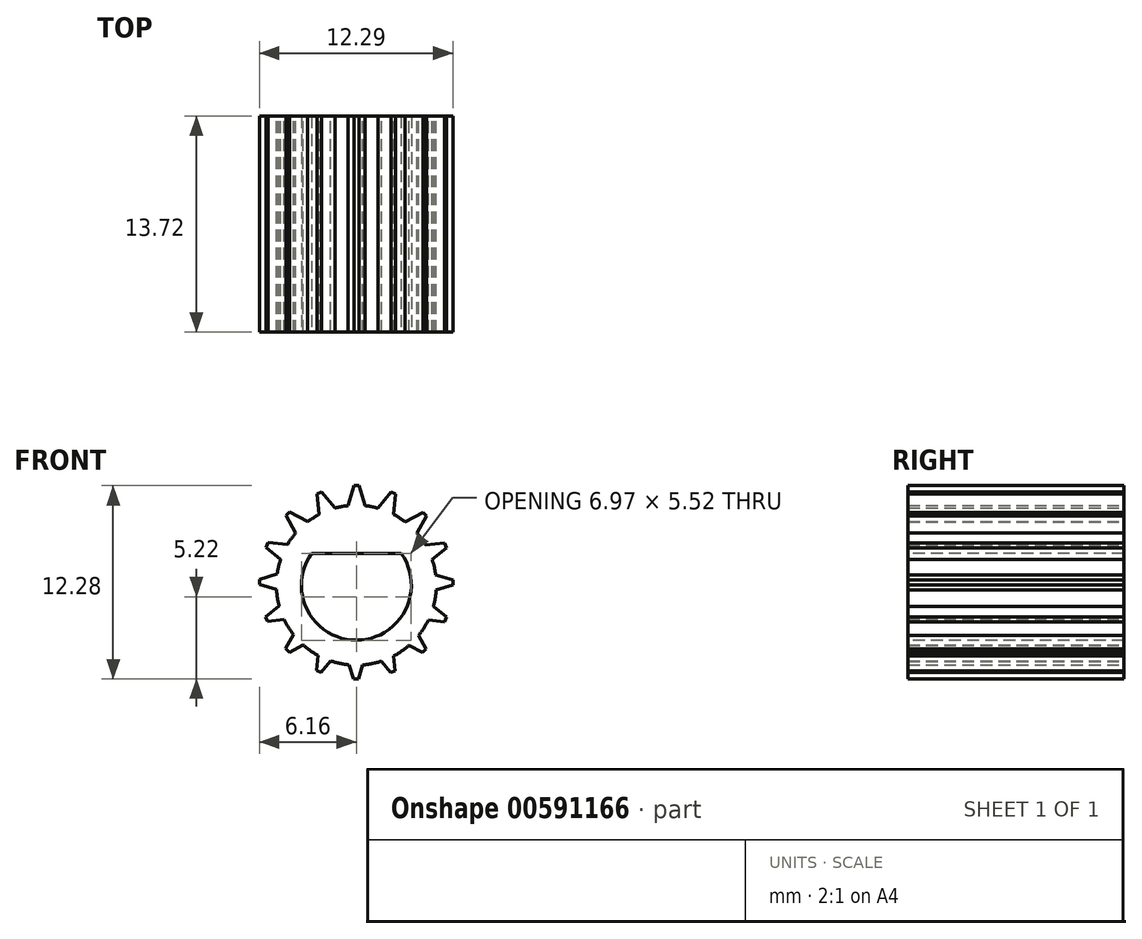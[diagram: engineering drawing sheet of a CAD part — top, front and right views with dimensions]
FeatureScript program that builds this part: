
annotation { "Feature Type Name" : "Feature", "Feature Type Description" : "" }
export const myFeature = defineFeature(function(context is Context, id is Id, definition is map)
    precondition{}
    {
        {
            var Q0;
            Q0=qCreatedBy(makeId("Front.planeOp"),FACE);
            var sketch = newSketch(context, id + "F0", { "sketchPlane" : qUnion([Q0])});
            skCircle(sketch, "E0", {"center": v(0, 0) * mm, "radius": 6.25 * mm});
            skLineSegment(sketch, "E1", {"start": v(0, 0) * mm, "end": v(0, 6.25) * mm, "construction": true});
            skLineSegment(sketch, "E2", {"start": v(0, 6.25) * mm, "end": v(0, 9.25) * mm});
            skLineSegment(sketch, "E3", {"start": v(0, 9.25) * mm, "end": v(-0.96, 9.25) * mm});
            skLineSegment(sketch, "E4", {"start": v(-0.96, 9.25) * mm, "end": v(-2.3, 5.81) * mm});
            skLineSegment(sketch, "E5.MirrorCS", {"start": v(0, 9.25) * mm, "end": v(0.96, 9.25) * mm});
            skLineSegment(sketch, "E6.MirrorCS", {"start": v(0.96, 9.25) * mm, "end": v(2.3, 5.81) * mm});
            skPoint(sketch, "E7.center", {"position": v(0, 1.25) * mm});
            skPoint(sketch, "E8.center", {"position": v(0, -1) * mm});
            skLineSegment(sketch, "E9.1.0", {"start": v(-8.5, 3.8) * mm, "end": v(-6.18, 0.91) * mm});
            skLineSegment(sketch, "E9.1.1", {"start": v(-8.01, 4.62) * mm, "end": v(-8.5, 3.8) * mm});
            skLineSegment(sketch, "E9.1.2", {"start": v(-7.53, 5.46) * mm, "end": v(-3.88, 4.9) * mm});
            skLineSegment(sketch, "E9.1.3", {"start": v(-8.01, 4.62) * mm, "end": v(-7.53, 5.46) * mm});
            skLineSegment(sketch, "E9.2.0", {"start": v(-7.53, -5.46) * mm, "end": v(-3.88, -4.9) * mm});
            skLineSegment(sketch, "E9.2.1", {"start": v(-8.01, -4.63) * mm, "end": v(-7.53, -5.46) * mm});
            skLineSegment(sketch, "E9.2.2", {"start": v(-8.5, -3.8) * mm, "end": v(-6.18, -0.91) * mm});
            skLineSegment(sketch, "E9.2.3", {"start": v(-8.01, -4.63) * mm, "end": v(-8.5, -3.8) * mm});
            skLineSegment(sketch, "E9.3.0", {"start": v(0.96, -9.25) * mm, "end": v(2.3, -5.81) * mm});
            skLineSegment(sketch, "E9.3.1", {"start": v(0, -9.25) * mm, "end": v(0.96, -9.25) * mm});
            skLineSegment(sketch, "E9.3.2", {"start": v(-0.96, -9.25) * mm, "end": v(-2.3, -5.81) * mm});
            skLineSegment(sketch, "E9.3.3", {"start": v(0, -9.25) * mm, "end": v(-0.96, -9.25) * mm});
            skLineSegment(sketch, "E9.4.0", {"start": v(8.5, -3.8) * mm, "end": v(6.18, -0.91) * mm});
            skLineSegment(sketch, "E9.4.1", {"start": v(8.01, -4.63) * mm, "end": v(8.5, -3.8) * mm});
            skLineSegment(sketch, "E9.4.2", {"start": v(7.53, -5.46) * mm, "end": v(3.88, -4.9) * mm});
            skLineSegment(sketch, "E9.4.3", {"start": v(8.01, -4.63) * mm, "end": v(7.53, -5.46) * mm});
            skLineSegment(sketch, "E9.5.0", {"start": v(7.53, 5.46) * mm, "end": v(3.88, 4.9) * mm});
            skLineSegment(sketch, "E9.5.1", {"start": v(8.01, 4.63) * mm, "end": v(7.53, 5.46) * mm});
            skLineSegment(sketch, "E9.5.2", {"start": v(8.5, 3.8) * mm, "end": v(6.18, 0.91) * mm});
            skLineSegment(sketch, "E9.5.3", {"start": v(8.01, 4.63) * mm, "end": v(8.5, 3.8) * mm});
            skSolve(sketch);
        }
        {
            var Q0;
            Q0 = qSketchRegion(id + "F0", true);
            extrude(context, id + "F1", {"entities" : qUnion([Q0]), "depth" : 8.38 * mm, "offsetDistance" : 25.4 * mm});
        }
        {
            var Q0;
            Q0=makeQuery(id+"F1.opExtrude","CAP_FACE",FACE,{"disambiguationData":[OSD([sQuery(id+"F0.wireOp",EDGE,"E0"),sQuery(id+"F0.wireOp",EDGE,"E3"),sQuery(id+"F0.wireOp",EDGE,"E4"),sQuery(id+"F0.wireOp",EDGE,"E5.MirrorCS"),sQuery(id+"F0.wireOp",EDGE,"E6.MirrorCS"),sQuery(id+"F0.wireOp",EDGE,"E9.1.0"),sQuery(id+"F0.wireOp",EDGE,"E9.1.1"),sQuery(id+"F0.wireOp",EDGE,"E9.1.2"),sQuery(id+"F0.wireOp",EDGE,"E9.1.3"),sQuery(id+"F0.wireOp",EDGE,"E9.2.0"),sQuery(id+"F0.wireOp",EDGE,"E9.2.1"),sQuery(id+"F0.wireOp",EDGE,"E9.2.2"),sQuery(id+"F0.wireOp",EDGE,"E9.2.3"),sQuery(id+"F0.wireOp",EDGE,"E9.3.0"),sQuery(id+"F0.wireOp",EDGE,"E9.3.1"),sQuery(id+"F0.wireOp",EDGE,"E9.3.2"),sQuery(id+"F0.wireOp",EDGE,"E9.3.3"),sQuery(id+"F0.wireOp",EDGE,"E9.4.0"),sQuery(id+"F0.wireOp",EDGE,"E9.4.1"),sQuery(id+"F0.wireOp",EDGE,"E9.4.2"),sQuery(id+"F0.wireOp",EDGE,"E9.4.3"),sQuery(id+"F0.wireOp",EDGE,"E9.5.0"),sQuery(id+"F0.wireOp",EDGE,"E9.5.1"),sQuery(id+"F0.wireOp",EDGE,"E9.5.2"),sQuery(id+"F0.wireOp",EDGE,"E9.5.3")])],"isStart":false});
            var sketch = newSketch(context, id + "F2", { "sketchPlane" : qUnion([Q0])});
            skCircle(sketch, "E10", {"center": v(0, 0) * mm, "radius": 3.5 * mm});
            skSolve(sketch);
        }
        {
            var Q0;
            Q0=makeQuery(id+"F1.opExtrude","CAP_FACE",FACE,{"disambiguationData":[OSD([sQuery(id+"F0.wireOp",EDGE,"E0"),sQuery(id+"F0.wireOp",EDGE,"E3"),sQuery(id+"F0.wireOp",EDGE,"E4"),sQuery(id+"F0.wireOp",EDGE,"E5.MirrorCS"),sQuery(id+"F0.wireOp",EDGE,"E6.MirrorCS"),sQuery(id+"F0.wireOp",EDGE,"E9.1.0"),sQuery(id+"F0.wireOp",EDGE,"E9.1.1"),sQuery(id+"F0.wireOp",EDGE,"E9.1.2"),sQuery(id+"F0.wireOp",EDGE,"E9.1.3"),sQuery(id+"F0.wireOp",EDGE,"E9.2.0"),sQuery(id+"F0.wireOp",EDGE,"E9.2.1"),sQuery(id+"F0.wireOp",EDGE,"E9.2.2"),sQuery(id+"F0.wireOp",EDGE,"E9.2.3"),sQuery(id+"F0.wireOp",EDGE,"E9.3.0"),sQuery(id+"F0.wireOp",EDGE,"E9.3.1"),sQuery(id+"F0.wireOp",EDGE,"E9.3.2"),sQuery(id+"F0.wireOp",EDGE,"E9.3.3"),sQuery(id+"F0.wireOp",EDGE,"E9.4.0"),sQuery(id+"F0.wireOp",EDGE,"E9.4.1"),sQuery(id+"F0.wireOp",EDGE,"E9.4.2"),sQuery(id+"F0.wireOp",EDGE,"E9.4.3"),sQuery(id+"F0.wireOp",EDGE,"E9.5.0"),sQuery(id+"F0.wireOp",EDGE,"E9.5.1"),sQuery(id+"F0.wireOp",EDGE,"E9.5.2"),sQuery(id+"F0.wireOp",EDGE,"E9.5.3")])],"isStart":false});
            var sketch = newSketch(context, id + "F3", { "sketchPlane" : qUnion([Q0])});
            skCircle(sketch, "E11", {"center": v(0, 0) * mm, "radius": 5.08 * mm});
            skCircle(sketch, "E12", {"center": v(0, 0) * mm, "radius": 12.17 * mm});
            skSolve(sketch);
        }
        {
            var Q0;
            Q0 = qSketchRegion(id + "F2", true);
            extrude(context, id + "F4", {"entities" : qUnion([Q0]), "operationType" : NewBodyOperationType.REMOVE, "oppositeDirection" : true, "depth" : 25.4 * mm, "offsetDistance" : 25.4 * mm, "hasSecondDirection" : true, "secondDirectionOppositeDirection" : false, "secondDirectionDepth" : 25.4 * mm});
        }
        {
            var Q0;
            Q0=makeQuery(id+"F1.opExtrude","CAP_FACE",FACE,{"disambiguationData":[OSD([sQuery(id+"F0.wireOp",EDGE,"E0"),sQuery(id+"F0.wireOp",EDGE,"E3"),sQuery(id+"F0.wireOp",EDGE,"E4"),sQuery(id+"F0.wireOp",EDGE,"E5.MirrorCS"),sQuery(id+"F0.wireOp",EDGE,"E6.MirrorCS"),sQuery(id+"F0.wireOp",EDGE,"E9.1.0"),sQuery(id+"F0.wireOp",EDGE,"E9.1.1"),sQuery(id+"F0.wireOp",EDGE,"E9.1.2"),sQuery(id+"F0.wireOp",EDGE,"E9.1.3"),sQuery(id+"F0.wireOp",EDGE,"E9.2.0"),sQuery(id+"F0.wireOp",EDGE,"E9.2.1"),sQuery(id+"F0.wireOp",EDGE,"E9.2.2"),sQuery(id+"F0.wireOp",EDGE,"E9.2.3"),sQuery(id+"F0.wireOp",EDGE,"E9.3.0"),sQuery(id+"F0.wireOp",EDGE,"E9.3.1"),sQuery(id+"F0.wireOp",EDGE,"E9.3.2"),sQuery(id+"F0.wireOp",EDGE,"E9.3.3"),sQuery(id+"F0.wireOp",EDGE,"E9.4.0"),sQuery(id+"F0.wireOp",EDGE,"E9.4.1"),sQuery(id+"F0.wireOp",EDGE,"E9.4.2"),sQuery(id+"F0.wireOp",EDGE,"E9.4.3"),sQuery(id+"F0.wireOp",EDGE,"E9.5.0"),sQuery(id+"F0.wireOp",EDGE,"E9.5.1"),sQuery(id+"F0.wireOp",EDGE,"E9.5.2"),sQuery(id+"F0.wireOp",EDGE,"E9.5.3")])],"isStart":false});
            var sketch = newSketch(context, id + "F5", { "sketchPlane" : qUnion([Q0])});
            skSolve(sketch);
        }
        {
            var Q0;
            Q0 = qSketchRegion(id + "F5", true);
            var Q1;
            {var subQ18=sQuery(id+"F0.wireOp",EDGE,"E4");Q1=makeQuery(id+"F5.imprint","IMPRINT",FACE,{"disambiguationData":[TD([[makeQuery(id+"F5.imprint","IMPRINT",EDGE,{"derivedFrom":makeQuery(id+"F1.opExtrude","CAP_EDGE",EDGE,{"disambiguationData":[OSD([subQ18])],"isStart":false})}),1.0]])]});}
            extrude(context, id + "F6", {"entities" : qUnion([Q0, Q1]), "operationType" : NewBodyOperationType.ADD, "depth" : 17.02 * mm, "offsetDistance" : 25.4 * mm});
        }
        {
            var Q0;
            Q0 = qSketchRegion(id + "F3", true);
            extrude(context, id + "F7", {"entities" : qUnion([Q0]), "operationType" : NewBodyOperationType.REMOVE, "depth" : 8.64 * mm, "offsetDistance" : 25.4 * mm});
        }
        {
            var Q0;
            Q0=makeQuery(id+"F7.boolean.opBoolean","COPY",FACE,{"derivedFrom":makeQuery(id+"F7.opExtrude","CAP_FACE",FACE,{"disambiguationData":[OSD([sQuery(id+"F3.wireOp",EDGE,"E11"),sQuery(id+"F3.wireOp",EDGE,"E12")])],"isStart":true})});
            var sketch = newSketch(context, id + "F8", { "sketchPlane" : qUnion([Q0])});
            skLineSegment(sketch, "E13", {"start": v(0, 0) * mm, "end": v(0, 15.68) * mm, "construction": true});
            skLineSegment(sketch, "E14", {"start": v(-0.16, 6.33) * mm, "end": v(-0.54, 5.05) * mm});
            skLineSegment(sketch, "E15", {"start": v(-0.54, 5.05) * mm, "end": v(-0.52, 4.77) * mm});
            skLineSegment(sketch, "E16", {"start": v(-0.52, 4.77) * mm, "end": v(0, 4.77) * mm});
            skLineSegment(sketch, "E17", {"start": v(-0.16, 6.33) * mm, "end": v(0, 6.33) * mm});
            skLineSegment(sketch, "E18.MirrorCS", {"start": v(0.16, 6.33) * mm, "end": v(0, 6.33) * mm});
            skLineSegment(sketch, "E19.MirrorCS", {"start": v(0.16, 6.33) * mm, "end": v(0.54, 5.05) * mm});
            skLineSegment(sketch, "E20.MirrorCS", {"start": v(0.54, 5.05) * mm, "end": v(0.52, 4.77) * mm});
            skLineSegment(sketch, "E21.MirrorCS", {"start": v(0.52, 4.77) * mm, "end": v(0, 4.77) * mm});
            skLineSegment(sketch, "E22.1.0", {"start": v(-2.5, 5.8) * mm, "end": v(-2.35, 5.87) * mm});
            skLineSegment(sketch, "E22.1.1", {"start": v(-2.2, 5.93) * mm, "end": v(-2.35, 5.87) * mm});
            skLineSegment(sketch, "E22.1.2", {"start": v(-2.2, 5.93) * mm, "end": v(-1.36, 4.9) * mm});
            skLineSegment(sketch, "E22.1.3", {"start": v(-1.36, 4.9) * mm, "end": v(-1.27, 4.63) * mm});
            skLineSegment(sketch, "E22.1.4", {"start": v(-2.5, 5.8) * mm, "end": v(-2.36, 4.48) * mm});
            skLineSegment(sketch, "E22.1.5", {"start": v(-2.36, 4.48) * mm, "end": v(-2.24, 4.23) * mm});
            skLineSegment(sketch, "E22.1.6", {"start": v(-2.24, 4.23) * mm, "end": v(-1.76, 4.43) * mm});
            skLineSegment(sketch, "E22.1.7", {"start": v(-1.27, 4.63) * mm, "end": v(-1.76, 4.43) * mm});
            skLineSegment(sketch, "E22.2.0", {"start": v(-4.46, 4.43) * mm, "end": v(-4.35, 4.54) * mm});
            skLineSegment(sketch, "E22.2.1", {"start": v(-4.24, 4.66) * mm, "end": v(-4.35, 4.54) * mm});
            skLineSegment(sketch, "E22.2.2", {"start": v(-4.24, 4.66) * mm, "end": v(-3.06, 4.02) * mm});
            skLineSegment(sketch, "E22.2.3", {"start": v(-3.06, 4.02) * mm, "end": v(-2.88, 3.81) * mm});
            skLineSegment(sketch, "E22.2.4", {"start": v(-4.46, 4.43) * mm, "end": v(-3.82, 3.26) * mm});
            skLineSegment(sketch, "E22.2.5", {"start": v(-3.82, 3.26) * mm, "end": v(-3.62, 3.07) * mm});
            skLineSegment(sketch, "E22.2.6", {"start": v(-3.62, 3.07) * mm, "end": v(-3.25, 3.44) * mm});
            skLineSegment(sketch, "E22.2.7", {"start": v(-2.88, 3.81) * mm, "end": v(-3.25, 3.44) * mm});
            skLineSegment(sketch, "E22.3.0", {"start": v(-5.75, 2.4) * mm, "end": v(-5.68, 2.55) * mm});
            skLineSegment(sketch, "E22.3.1", {"start": v(-5.62, 2.7) * mm, "end": v(-5.68, 2.55) * mm});
            skLineSegment(sketch, "E22.3.2", {"start": v(-5.62, 2.7) * mm, "end": v(-4.3, 2.56) * mm});
            skLineSegment(sketch, "E22.3.3", {"start": v(-4.3, 2.56) * mm, "end": v(-4.05, 2.44) * mm});
            skLineSegment(sketch, "E22.3.4", {"start": v(-5.75, 2.4) * mm, "end": v(-4.7, 1.57) * mm});
            skLineSegment(sketch, "E22.3.5", {"start": v(-4.7, 1.57) * mm, "end": v(-4.45, 1.48) * mm});
            skLineSegment(sketch, "E22.3.6", {"start": v(-4.45, 1.48) * mm, "end": v(-4.25, 1.96) * mm});
            skLineSegment(sketch, "E22.3.7", {"start": v(-4.05, 2.44) * mm, "end": v(-4.25, 1.96) * mm});
            skLineSegment(sketch, "E22.4.0", {"start": v(-6.16, 0.05) * mm, "end": v(-6.16, 0.2) * mm});
            skLineSegment(sketch, "E22.4.1", {"start": v(-6.16, 0.36) * mm, "end": v(-6.16, 0.2) * mm});
            skLineSegment(sketch, "E22.4.2", {"start": v(-6.16, 0.36) * mm, "end": v(-4.88, 0.75) * mm});
            skLineSegment(sketch, "E22.4.3", {"start": v(-4.88, 0.75) * mm, "end": v(-4.6, 0.73) * mm});
            skLineSegment(sketch, "E22.4.4", {"start": v(-6.16, 0.05) * mm, "end": v(-4.88, -0.33) * mm});
            skLineSegment(sketch, "E22.4.5", {"start": v(-4.88, -0.33) * mm, "end": v(-4.6, -0.32) * mm});
            skLineSegment(sketch, "E22.4.6", {"start": v(-4.6, -0.32) * mm, "end": v(-4.6, 0.2) * mm});
            skLineSegment(sketch, "E22.4.7", {"start": v(-4.6, 0.73) * mm, "end": v(-4.6, 0.2) * mm});
            skLineSegment(sketch, "E22.5.0", {"start": v(-5.64, -2.3) * mm, "end": v(-5.7, -2.15) * mm});
            skLineSegment(sketch, "E22.5.1", {"start": v(-5.76, -2) * mm, "end": v(-5.7, -2.15) * mm});
            skLineSegment(sketch, "E22.5.2", {"start": v(-5.76, -2) * mm, "end": v(-4.72, -1.16) * mm});
            skLineSegment(sketch, "E22.5.3", {"start": v(-4.72, -1.16) * mm, "end": v(-4.46, -1.07) * mm});
            skLineSegment(sketch, "E22.5.4", {"start": v(-5.64, -2.3) * mm, "end": v(-4.3, -2.16) * mm});
            skLineSegment(sketch, "E22.5.5", {"start": v(-4.3, -2.16) * mm, "end": v(-4.06, -2.03) * mm});
            skLineSegment(sketch, "E22.5.6", {"start": v(-4.06, -2.03) * mm, "end": v(-4.26, -1.55) * mm});
            skLineSegment(sketch, "E22.5.7", {"start": v(-4.46, -1.07) * mm, "end": v(-4.26, -1.55) * mm});
            skLineSegment(sketch, "E22.6.0", {"start": v(-4.26, -4.25) * mm, "end": v(-4.37, -4.14) * mm});
            skLineSegment(sketch, "E22.6.1", {"start": v(-4.48, -4.03) * mm, "end": v(-4.37, -4.14) * mm});
            skLineSegment(sketch, "E22.6.2", {"start": v(-4.48, -4.03) * mm, "end": v(-3.85, -2.86) * mm});
            skLineSegment(sketch, "E22.6.3", {"start": v(-3.85, -2.86) * mm, "end": v(-3.64, -2.67) * mm});
            skLineSegment(sketch, "E22.6.4", {"start": v(-4.26, -4.25) * mm, "end": v(-3.08, -3.62) * mm});
            skLineSegment(sketch, "E22.6.5", {"start": v(-3.08, -3.62) * mm, "end": v(-2.9, -3.41) * mm});
            skLineSegment(sketch, "E22.6.6", {"start": v(-2.9, -3.41) * mm, "end": v(-3.27, -3.04) * mm});
            skLineSegment(sketch, "E22.6.7", {"start": v(-3.64, -2.67) * mm, "end": v(-3.27, -3.04) * mm});
            skLineSegment(sketch, "E22.7.0", {"start": v(-2.23, -5.54) * mm, "end": v(-2.38, -5.48) * mm});
            skLineSegment(sketch, "E22.7.1", {"start": v(-2.53, -5.42) * mm, "end": v(-2.38, -5.48) * mm});
            skLineSegment(sketch, "E22.7.2", {"start": v(-2.53, -5.42) * mm, "end": v(-2.39, -4.09) * mm});
            skLineSegment(sketch, "E22.7.3", {"start": v(-2.39, -4.09) * mm, "end": v(-2.27, -3.84) * mm});
            skLineSegment(sketch, "E22.7.4", {"start": v(-2.23, -5.54) * mm, "end": v(-1.4, -4.5) * mm});
            skLineSegment(sketch, "E22.7.5", {"start": v(-1.4, -4.5) * mm, "end": v(-1.3, -4.24) * mm});
            skLineSegment(sketch, "E22.7.6", {"start": v(-1.3, -4.24) * mm, "end": v(-1.78, -4.04) * mm});
            skLineSegment(sketch, "E22.7.7", {"start": v(-2.27, -3.84) * mm, "end": v(-1.78, -4.04) * mm});
            skLineSegment(sketch, "E22.8.0", {"start": v(0.13, -5.95) * mm, "end": v(-0.03, -5.95) * mm});
            skLineSegment(sketch, "E22.8.1", {"start": v(-0.19, -5.95) * mm, "end": v(-0.03, -5.95) * mm});
            skLineSegment(sketch, "E22.8.2", {"start": v(-0.19, -5.95) * mm, "end": v(-0.57, -4.67) * mm});
            skLineSegment(sketch, "E22.8.3", {"start": v(-0.57, -4.67) * mm, "end": v(-0.55, -4.4) * mm});
            skLineSegment(sketch, "E22.8.4", {"start": v(0.13, -5.95) * mm, "end": v(0.5, -4.67) * mm});
            skLineSegment(sketch, "E22.8.5", {"start": v(0.5, -4.67) * mm, "end": v(0.49, -4.4) * mm});
            skLineSegment(sketch, "E22.8.6", {"start": v(0.49, -4.4) * mm, "end": v(-0.03, -4.4) * mm});
            skLineSegment(sketch, "E22.8.7", {"start": v(-0.55, -4.4) * mm, "end": v(-0.03, -4.4) * mm});
            skLineSegment(sketch, "E22.9.0", {"start": v(2.47, -5.43) * mm, "end": v(2.32, -5.5) * mm});
            skLineSegment(sketch, "E22.9.1", {"start": v(2.17, -5.55) * mm, "end": v(2.32, -5.5) * mm});
            skLineSegment(sketch, "E22.9.2", {"start": v(2.17, -5.55) * mm, "end": v(1.33, -4.51) * mm});
            skLineSegment(sketch, "E22.9.3", {"start": v(1.33, -4.51) * mm, "end": v(1.24, -4.25) * mm});
            skLineSegment(sketch, "E22.9.4", {"start": v(2.47, -5.43) * mm, "end": v(2.33, -4.1) * mm});
            skLineSegment(sketch, "E22.9.5", {"start": v(2.33, -4.1) * mm, "end": v(2.2, -3.85) * mm});
            skLineSegment(sketch, "E22.9.6", {"start": v(2.2, -3.85) * mm, "end": v(1.72, -4.05) * mm});
            skLineSegment(sketch, "E22.9.7", {"start": v(1.24, -4.25) * mm, "end": v(1.72, -4.05) * mm});
            skLineSegment(sketch, "E22.10.0", {"start": v(4.43, -4.05) * mm, "end": v(4.32, -4.16) * mm});
            skLineSegment(sketch, "E22.10.1", {"start": v(4.2, -4.28) * mm, "end": v(4.32, -4.16) * mm});
            skLineSegment(sketch, "E22.10.2", {"start": v(4.2, -4.28) * mm, "end": v(3.03, -3.64) * mm});
            skLineSegment(sketch, "E22.10.3", {"start": v(3.03, -3.64) * mm, "end": v(2.85, -3.43) * mm});
            skLineSegment(sketch, "E22.10.4", {"start": v(4.43, -4.05) * mm, "end": v(3.8, -2.88) * mm});
            skLineSegment(sketch, "E22.10.5", {"start": v(3.8, -2.88) * mm, "end": v(3.58, -2.7) * mm});
            skLineSegment(sketch, "E22.10.6", {"start": v(3.58, -2.7) * mm, "end": v(3.22, -3.06) * mm});
            skLineSegment(sketch, "E22.10.7", {"start": v(2.85, -3.43) * mm, "end": v(3.22, -3.06) * mm});
            skLineSegment(sketch, "E22.11.0", {"start": v(5.71, -2.03) * mm, "end": v(5.65, -2.18) * mm});
            skLineSegment(sketch, "E22.11.1", {"start": v(5.6, -2.32) * mm, "end": v(5.65, -2.18) * mm});
            skLineSegment(sketch, "E22.11.2", {"start": v(5.6, -2.32) * mm, "end": v(4.26, -2.18) * mm});
            skLineSegment(sketch, "E22.11.3", {"start": v(4.26, -2.18) * mm, "end": v(4.01, -2.06) * mm});
            skLineSegment(sketch, "E22.11.4", {"start": v(5.71, -2.03) * mm, "end": v(4.68, -1.19) * mm});
            skLineSegment(sketch, "E22.11.5", {"start": v(4.68, -1.19) * mm, "end": v(4.41, -1.1) * mm});
            skLineSegment(sketch, "E22.11.6", {"start": v(4.41, -1.1) * mm, "end": v(4.21, -1.58) * mm});
            skLineSegment(sketch, "E22.11.7", {"start": v(4.01, -2.06) * mm, "end": v(4.21, -1.58) * mm});
            skPoint(sketch, "E22.center", {"position": v(-0.02, 0.19) * mm});
            skLineSegment(sketch, "E23.1.12.0", {"start": v(6.13, 0.33) * mm, "end": v(6.13, 0.17) * mm});
            skLineSegment(sketch, "E23.3.12.0", {"start": v(6.13, 0.02) * mm, "end": v(6.13, 0.17) * mm});
            skLineSegment(sketch, "E23.6.12.0", {"start": v(6.13, 0.02) * mm, "end": v(4.85, -0.37) * mm});
            skLineSegment(sketch, "E23.9.12.0", {"start": v(4.85, -0.37) * mm, "end": v(4.57, -0.35) * mm});
            skLineSegment(sketch, "E23.12.12.0", {"start": v(6.13, 0.33) * mm, "end": v(4.85, 0.71) * mm});
            skLineSegment(sketch, "E23.15.12.0", {"start": v(4.85, 0.71) * mm, "end": v(4.57, 0.7) * mm});
            skLineSegment(sketch, "E23.18.12.0", {"start": v(4.57, 0.7) * mm, "end": v(4.57, 0.17) * mm});
            skLineSegment(sketch, "E23.21.12.0", {"start": v(4.57, -0.35) * mm, "end": v(4.57, 0.17) * mm});
            skLineSegment(sketch, "E23.1.13.0", {"start": v(5.6, 2.67) * mm, "end": v(5.67, 2.53) * mm});
            skLineSegment(sketch, "E23.3.13.0", {"start": v(5.73, 2.38) * mm, "end": v(5.67, 2.53) * mm});
            skLineSegment(sketch, "E23.6.13.0", {"start": v(5.73, 2.38) * mm, "end": v(4.69, 1.54) * mm});
            skLineSegment(sketch, "E23.9.13.0", {"start": v(4.69, 1.54) * mm, "end": v(4.43, 1.45) * mm});
            skLineSegment(sketch, "E23.12.13.0", {"start": v(5.6, 2.67) * mm, "end": v(4.28, 2.53) * mm});
            skLineSegment(sketch, "E23.15.13.0", {"start": v(4.28, 2.53) * mm, "end": v(4.03, 2.41) * mm});
            skLineSegment(sketch, "E23.18.13.0", {"start": v(4.03, 2.41) * mm, "end": v(4.23, 1.93) * mm});
            skLineSegment(sketch, "E23.21.13.0", {"start": v(4.43, 1.45) * mm, "end": v(4.23, 1.93) * mm});
            skLineSegment(sketch, "E23.1.14.0", {"start": v(4.23, 4.63) * mm, "end": v(4.34, 4.52) * mm});
            skLineSegment(sketch, "E23.3.14.0", {"start": v(4.45, 4.4) * mm, "end": v(4.34, 4.52) * mm});
            skLineSegment(sketch, "E23.6.14.0", {"start": v(4.45, 4.4) * mm, "end": v(3.82, 3.23) * mm});
            skLineSegment(sketch, "E23.9.14.0", {"start": v(3.82, 3.23) * mm, "end": v(3.6, 3.05) * mm});
            skLineSegment(sketch, "E23.12.14.0", {"start": v(4.23, 4.63) * mm, "end": v(3.05, 4) * mm});
            skLineSegment(sketch, "E23.15.14.0", {"start": v(3.05, 4) * mm, "end": v(2.87, 3.79) * mm});
            skLineSegment(sketch, "E23.18.14.0", {"start": v(2.87, 3.79) * mm, "end": v(3.24, 3.42) * mm});
            skLineSegment(sketch, "E23.21.14.0", {"start": v(3.6, 3.05) * mm, "end": v(3.24, 3.42) * mm});
            skLineSegment(sketch, "E23.1.15.0", {"start": v(2.2, 5.92) * mm, "end": v(2.35, 5.86) * mm});
            skLineSegment(sketch, "E23.3.15.0", {"start": v(2.5, 5.8) * mm, "end": v(2.35, 5.86) * mm});
            skLineSegment(sketch, "E23.6.15.0", {"start": v(2.5, 5.8) * mm, "end": v(2.36, 4.47) * mm});
            skLineSegment(sketch, "E23.9.15.0", {"start": v(2.36, 4.47) * mm, "end": v(2.24, 4.22) * mm});
            skLineSegment(sketch, "E23.12.15.0", {"start": v(2.2, 5.92) * mm, "end": v(1.36, 4.88) * mm});
            skLineSegment(sketch, "E23.15.15.0", {"start": v(1.36, 4.88) * mm, "end": v(1.27, 4.62) * mm});
            skLineSegment(sketch, "E23.18.15.0", {"start": v(1.27, 4.62) * mm, "end": v(1.75, 4.42) * mm});
            skLineSegment(sketch, "E23.21.15.0", {"start": v(2.24, 4.22) * mm, "end": v(1.75, 4.42) * mm});
            skSolve(sketch);
        }
        {
            var Q0;
            Q0 = qSketchRegion(id + "F8", true);
            extrude(context, id + "F9", {"entities" : qUnion([Q0]), "operationType" : NewBodyOperationType.ADD, "depth" : 8.64 * mm, "offsetDistance" : 25.4 * mm});
        }
        {
            var Q0;
            Q0=makeQuery(id+"F6.opExtrude","CAP_FACE",FACE,{"disambiguationData":[OSD([sQuery(id+"F0.wireOp",EDGE,"E0"),sQuery(id+"F0.wireOp",EDGE,"E3"),sQuery(id+"F0.wireOp",EDGE,"E4"),sQuery(id+"F0.wireOp",EDGE,"E5.MirrorCS"),sQuery(id+"F0.wireOp",EDGE,"E6.MirrorCS"),sQuery(id+"F0.wireOp",EDGE,"E9.1.0"),sQuery(id+"F0.wireOp",EDGE,"E9.1.1"),sQuery(id+"F0.wireOp",EDGE,"E9.1.2"),sQuery(id+"F0.wireOp",EDGE,"E9.1.3"),sQuery(id+"F0.wireOp",EDGE,"E9.2.0"),sQuery(id+"F0.wireOp",EDGE,"E9.2.1"),sQuery(id+"F0.wireOp",EDGE,"E9.2.2"),sQuery(id+"F0.wireOp",EDGE,"E9.2.3"),sQuery(id+"F0.wireOp",EDGE,"E9.3.0"),sQuery(id+"F0.wireOp",EDGE,"E9.3.1"),sQuery(id+"F0.wireOp",EDGE,"E9.3.2"),sQuery(id+"F0.wireOp",EDGE,"E9.3.3"),sQuery(id+"F0.wireOp",EDGE,"E9.4.0"),sQuery(id+"F0.wireOp",EDGE,"E9.4.1"),sQuery(id+"F0.wireOp",EDGE,"E9.4.2"),sQuery(id+"F0.wireOp",EDGE,"E9.4.3"),sQuery(id+"F0.wireOp",EDGE,"E9.5.0"),sQuery(id+"F0.wireOp",EDGE,"E9.5.1"),sQuery(id+"F0.wireOp",EDGE,"E9.5.2"),sQuery(id+"F0.wireOp",EDGE,"E9.5.3"),sQuery(id+"F2.wireOp",EDGE,"E10")])],"isStart":false});
            extrude(context, id + "F10", {"entities" : qUnion([Q0]), "operationType" : NewBodyOperationType.REMOVE, "oppositeDirection" : true, "depth" : 8.38 * mm, "offsetDistance" : 25.4 * mm});
        }
        {
            var Q0;
            Q0=makeQuery(id+"F1.opExtrude","CAP_FACE",FACE,{"disambiguationData":[OSD([sQuery(id+"F0.wireOp",EDGE,"E0"),sQuery(id+"F0.wireOp",EDGE,"E3"),sQuery(id+"F0.wireOp",EDGE,"E4"),sQuery(id+"F0.wireOp",EDGE,"E5.MirrorCS"),sQuery(id+"F0.wireOp",EDGE,"E6.MirrorCS"),sQuery(id+"F0.wireOp",EDGE,"E9.1.0"),sQuery(id+"F0.wireOp",EDGE,"E9.1.1"),sQuery(id+"F0.wireOp",EDGE,"E9.1.2"),sQuery(id+"F0.wireOp",EDGE,"E9.1.3"),sQuery(id+"F0.wireOp",EDGE,"E9.2.0"),sQuery(id+"F0.wireOp",EDGE,"E9.2.1"),sQuery(id+"F0.wireOp",EDGE,"E9.2.2"),sQuery(id+"F0.wireOp",EDGE,"E9.2.3"),sQuery(id+"F0.wireOp",EDGE,"E9.3.0"),sQuery(id+"F0.wireOp",EDGE,"E9.3.1"),sQuery(id+"F0.wireOp",EDGE,"E9.3.2"),sQuery(id+"F0.wireOp",EDGE,"E9.3.3"),sQuery(id+"F0.wireOp",EDGE,"E9.4.0"),sQuery(id+"F0.wireOp",EDGE,"E9.4.1"),sQuery(id+"F0.wireOp",EDGE,"E9.4.2"),sQuery(id+"F0.wireOp",EDGE,"E9.4.3"),sQuery(id+"F0.wireOp",EDGE,"E9.5.0"),sQuery(id+"F0.wireOp",EDGE,"E9.5.1"),sQuery(id+"F0.wireOp",EDGE,"E9.5.2"),sQuery(id+"F0.wireOp",EDGE,"E9.5.3")])],"isStart":true});
            extrude(context, id + "F11", {"entities" : qUnion([Q0]), "operationType" : NewBodyOperationType.REMOVE, "oppositeDirection" : true, "depth" : 8.38 * mm, "offsetDistance" : 25.4 * mm});
        }
        {
            var Q0;
            Q0=makeQuery(id+"F11.boolean.opBoolean","MERGE",FACE,{"derivedFrom":[makeQuery(id+"F9.opExtrude","CAP_FACE",FACE,{"disambiguationData":[OSD([sQuery(id+"F8.wireOp",EDGE,"E22.1.0"),sQuery(id+"F8.wireOp",EDGE,"E22.1.1"),sQuery(id+"F8.wireOp",EDGE,"E22.1.2"),sQuery(id+"F8.wireOp",EDGE,"E22.1.3"),sQuery(id+"F8.wireOp",EDGE,"E22.1.4"),sQuery(id+"F8.wireOp",EDGE,"E22.1.5"),sQuery(id+"F8.wireOp",EDGE,"E22.1.6"),sQuery(id+"F8.wireOp",EDGE,"E22.1.7")])],"isStart":true}),makeQuery(id+"F9.opExtrude","CAP_FACE",FACE,{"disambiguationData":[OSD([sQuery(id+"F8.wireOp",EDGE,"E22.4.0"),sQuery(id+"F8.wireOp",EDGE,"E22.4.1"),sQuery(id+"F8.wireOp",EDGE,"E22.4.2"),sQuery(id+"F8.wireOp",EDGE,"E22.4.3"),sQuery(id+"F8.wireOp",EDGE,"E22.4.4"),sQuery(id+"F8.wireOp",EDGE,"E22.4.5"),sQuery(id+"F8.wireOp",EDGE,"E22.4.6"),sQuery(id+"F8.wireOp",EDGE,"E22.4.7")])],"isStart":true}),makeQuery(id+"F9.opExtrude","CAP_FACE",FACE,{"disambiguationData":[OSD([sQuery(id+"F8.wireOp",EDGE,"E22.6.0"),sQuery(id+"F8.wireOp",EDGE,"E22.6.1"),sQuery(id+"F8.wireOp",EDGE,"E22.6.2"),sQuery(id+"F8.wireOp",EDGE,"E22.6.3"),sQuery(id+"F8.wireOp",EDGE,"E22.6.4"),sQuery(id+"F8.wireOp",EDGE,"E22.6.5"),sQuery(id+"F8.wireOp",EDGE,"E22.6.6"),sQuery(id+"F8.wireOp",EDGE,"E22.6.7")])],"isStart":true}),makeQuery(id+"F9.opExtrude","CAP_FACE",FACE,{"disambiguationData":[OSD([sQuery(id+"F8.wireOp",EDGE,"E22.8.0"),sQuery(id+"F8.wireOp",EDGE,"E22.8.1"),sQuery(id+"F8.wireOp",EDGE,"E22.8.2"),sQuery(id+"F8.wireOp",EDGE,"E22.8.3"),sQuery(id+"F8.wireOp",EDGE,"E22.8.4"),sQuery(id+"F8.wireOp",EDGE,"E22.8.5"),sQuery(id+"F8.wireOp",EDGE,"E22.8.6"),sQuery(id+"F8.wireOp",EDGE,"E22.8.7")])],"isStart":true}),makeQuery(id+"F9.opExtrude","CAP_FACE",FACE,{"disambiguationData":[OSD([sQuery(id+"F8.wireOp",EDGE,"E22.10.0"),sQuery(id+"F8.wireOp",EDGE,"E22.10.1"),sQuery(id+"F8.wireOp",EDGE,"E22.10.2"),sQuery(id+"F8.wireOp",EDGE,"E22.10.3"),sQuery(id+"F8.wireOp",EDGE,"E22.10.4"),sQuery(id+"F8.wireOp",EDGE,"E22.10.5"),sQuery(id+"F8.wireOp",EDGE,"E22.10.6"),sQuery(id+"F8.wireOp",EDGE,"E22.10.7")])],"isStart":true}),makeQuery(id+"F9.opExtrude","CAP_FACE",FACE,{"disambiguationData":[OSD([sQuery(id+"F8.wireOp",EDGE,"E22.13.0"),sQuery(id+"F8.wireOp",EDGE,"E22.13.1"),sQuery(id+"F8.wireOp",EDGE,"E22.13.2"),sQuery(id+"F8.wireOp",EDGE,"E22.13.3"),sQuery(id+"F8.wireOp",EDGE,"E22.13.4"),sQuery(id+"F8.wireOp",EDGE,"E22.13.5"),sQuery(id+"F8.wireOp",EDGE,"E22.13.6"),sQuery(id+"F8.wireOp",EDGE,"E22.13.7")])],"isStart":true}),makeQuery(id+"F11.opExtrude","CAP_FACE",FACE,{"disambiguationData":[OSD([sQuery(id+"F0.wireOp",EDGE,"E0"),sQuery(id+"F0.wireOp",EDGE,"E3"),sQuery(id+"F0.wireOp",EDGE,"E4"),sQuery(id+"F0.wireOp",EDGE,"E5.MirrorCS"),sQuery(id+"F0.wireOp",EDGE,"E6.MirrorCS"),sQuery(id+"F0.wireOp",EDGE,"E9.1.0"),sQuery(id+"F0.wireOp",EDGE,"E9.1.1"),sQuery(id+"F0.wireOp",EDGE,"E9.1.2"),sQuery(id+"F0.wireOp",EDGE,"E9.1.3"),sQuery(id+"F0.wireOp",EDGE,"E9.2.0"),sQuery(id+"F0.wireOp",EDGE,"E9.2.1"),sQuery(id+"F0.wireOp",EDGE,"E9.2.2"),sQuery(id+"F0.wireOp",EDGE,"E9.2.3"),sQuery(id+"F0.wireOp",EDGE,"E9.3.0"),sQuery(id+"F0.wireOp",EDGE,"E9.3.1"),sQuery(id+"F0.wireOp",EDGE,"E9.3.2"),sQuery(id+"F0.wireOp",EDGE,"E9.3.3"),sQuery(id+"F0.wireOp",EDGE,"E9.4.0"),sQuery(id+"F0.wireOp",EDGE,"E9.4.1"),sQuery(id+"F0.wireOp",EDGE,"E9.4.2"),sQuery(id+"F0.wireOp",EDGE,"E9.4.3"),sQuery(id+"F0.wireOp",EDGE,"E9.5.0"),sQuery(id+"F0.wireOp",EDGE,"E9.5.1"),sQuery(id+"F0.wireOp",EDGE,"E9.5.2"),sQuery(id+"F0.wireOp",EDGE,"E9.5.3")])],"isStart":false})]});
            extrude(context, id + "F12", {"entities" : qUnion([Q0]), "operationType" : NewBodyOperationType.ADD, "depth" : 5.08 * mm, "offsetDistance" : 25.4 * mm});
        }
        {
            var Q0;
            Q0=makeQuery(id+"F12.opExtrude","CAP_FACE",FACE,{"disambiguationData":[OSD([sQuery(id+"F0.wireOp",EDGE,"E0"),sQuery(id+"F0.wireOp",EDGE,"E3"),sQuery(id+"F0.wireOp",EDGE,"E4"),sQuery(id+"F0.wireOp",EDGE,"E5.MirrorCS"),sQuery(id+"F0.wireOp",EDGE,"E6.MirrorCS"),sQuery(id+"F0.wireOp",EDGE,"E9.1.0"),sQuery(id+"F0.wireOp",EDGE,"E9.1.1"),sQuery(id+"F0.wireOp",EDGE,"E9.1.2"),sQuery(id+"F0.wireOp",EDGE,"E9.1.3"),sQuery(id+"F0.wireOp",EDGE,"E9.2.0"),sQuery(id+"F0.wireOp",EDGE,"E9.2.1"),sQuery(id+"F0.wireOp",EDGE,"E9.2.2"),sQuery(id+"F0.wireOp",EDGE,"E9.2.3"),sQuery(id+"F0.wireOp",EDGE,"E9.3.0"),sQuery(id+"F0.wireOp",EDGE,"E9.3.1"),sQuery(id+"F0.wireOp",EDGE,"E9.3.2"),sQuery(id+"F0.wireOp",EDGE,"E9.3.3"),sQuery(id+"F0.wireOp",EDGE,"E9.4.0"),sQuery(id+"F0.wireOp",EDGE,"E9.4.1"),sQuery(id+"F0.wireOp",EDGE,"E9.4.2"),sQuery(id+"F0.wireOp",EDGE,"E9.4.3"),sQuery(id+"F0.wireOp",EDGE,"E9.5.0"),sQuery(id+"F0.wireOp",EDGE,"E9.5.1"),sQuery(id+"F0.wireOp",EDGE,"E9.5.2"),sQuery(id+"F0.wireOp",EDGE,"E9.5.3"),sQuery(id+"F8.wireOp",EDGE,"E22.1.0"),sQuery(id+"F8.wireOp",EDGE,"E22.1.1"),sQuery(id+"F8.wireOp",EDGE,"E22.1.2"),sQuery(id+"F8.wireOp",EDGE,"E22.1.3"),sQuery(id+"F8.wireOp",EDGE,"E22.1.4"),sQuery(id+"F8.wireOp",EDGE,"E22.1.5"),sQuery(id+"F8.wireOp",EDGE,"E22.1.6"),sQuery(id+"F8.wireOp",EDGE,"E22.1.7"),sQuery(id+"F8.wireOp",EDGE,"E22.4.0"),sQuery(id+"F8.wireOp",EDGE,"E22.4.1"),sQuery(id+"F8.wireOp",EDGE,"E22.4.2"),sQuery(id+"F8.wireOp",EDGE,"E22.4.3"),sQuery(id+"F8.wireOp",EDGE,"E22.4.4"),sQuery(id+"F8.wireOp",EDGE,"E22.4.5"),sQuery(id+"F8.wireOp",EDGE,"E22.4.6"),sQuery(id+"F8.wireOp",EDGE,"E22.4.7"),sQuery(id+"F8.wireOp",EDGE,"E22.6.0"),sQuery(id+"F8.wireOp",EDGE,"E22.6.1"),sQuery(id+"F8.wireOp",EDGE,"E22.6.2"),sQuery(id+"F8.wireOp",EDGE,"E22.6.3"),sQuery(id+"F8.wireOp",EDGE,"E22.6.4"),sQuery(id+"F8.wireOp",EDGE,"E22.6.5"),sQuery(id+"F8.wireOp",EDGE,"E22.6.6"),sQuery(id+"F8.wireOp",EDGE,"E22.6.7"),sQuery(id+"F8.wireOp",EDGE,"E22.8.0"),sQuery(id+"F8.wireOp",EDGE,"E22.8.1"),sQuery(id+"F8.wireOp",EDGE,"E22.8.2"),sQuery(id+"F8.wireOp",EDGE,"E22.8.3"),sQuery(id+"F8.wireOp",EDGE,"E22.8.4"),sQuery(id+"F8.wireOp",EDGE,"E22.8.5"),sQuery(id+"F8.wireOp",EDGE,"E22.8.6"),sQuery(id+"F8.wireOp",EDGE,"E22.8.7"),sQuery(id+"F8.wireOp",EDGE,"E22.10.0"),sQuery(id+"F8.wireOp",EDGE,"E22.10.1"),sQuery(id+"F8.wireOp",EDGE,"E22.10.2"),sQuery(id+"F8.wireOp",EDGE,"E22.10.3"),sQuery(id+"F8.wireOp",EDGE,"E22.10.4"),sQuery(id+"F8.wireOp",EDGE,"E22.10.5"),sQuery(id+"F8.wireOp",EDGE,"E22.10.6"),sQuery(id+"F8.wireOp",EDGE,"E22.10.7"),sQuery(id+"F8.wireOp",EDGE,"E22.13.0"),sQuery(id+"F8.wireOp",EDGE,"E22.13.1"),sQuery(id+"F8.wireOp",EDGE,"E22.13.2"),sQuery(id+"F8.wireOp",EDGE,"E22.13.3"),sQuery(id+"F8.wireOp",EDGE,"E22.13.4"),sQuery(id+"F8.wireOp",EDGE,"E22.13.5"),sQuery(id+"F8.wireOp",EDGE,"E22.13.6"),sQuery(id+"F8.wireOp",EDGE,"E22.13.7")])],"isStart":false});
            var sketch = newSketch(context, id + "F13", { "sketchPlane" : qUnion([Q0])});
            skArc(sketch, "E24", {"start": v(3.05, 2.03) * mm, "mid": v(0, 3.67) * mm, "end": v(-3.05, 2.03) * mm});
            skLineSegment(sketch, "E25", {"start": v(-3.05, 2.03) * mm, "end": v(3.05, 2.03) * mm});
            skSolve(sketch);
        }
        {
            var Q0;
            Q0 = qSketchRegion(id + "F13", true);
            var Q1;
            Q1=makeQuery(id+"F10.boolean.opBoolean","MERGE",FACE,{"derivedFrom":[makeQuery(id+"F9.opExtrude","CAP_FACE",FACE,{"disambiguationData":[OSD([sQuery(id+"F8.wireOp",EDGE,"E22.1.0"),sQuery(id+"F8.wireOp",EDGE,"E22.1.1"),sQuery(id+"F8.wireOp",EDGE,"E22.1.2"),sQuery(id+"F8.wireOp",EDGE,"E22.1.3"),sQuery(id+"F8.wireOp",EDGE,"E22.1.4"),sQuery(id+"F8.wireOp",EDGE,"E22.1.5"),sQuery(id+"F8.wireOp",EDGE,"E22.1.6"),sQuery(id+"F8.wireOp",EDGE,"E22.1.7")])],"isStart":false}),makeQuery(id+"F9.opExtrude","CAP_FACE",FACE,{"disambiguationData":[OSD([sQuery(id+"F8.wireOp",EDGE,"E22.4.0"),sQuery(id+"F8.wireOp",EDGE,"E22.4.1"),sQuery(id+"F8.wireOp",EDGE,"E22.4.2"),sQuery(id+"F8.wireOp",EDGE,"E22.4.3"),sQuery(id+"F8.wireOp",EDGE,"E22.4.4"),sQuery(id+"F8.wireOp",EDGE,"E22.4.5"),sQuery(id+"F8.wireOp",EDGE,"E22.4.6"),sQuery(id+"F8.wireOp",EDGE,"E22.4.7")])],"isStart":false}),makeQuery(id+"F9.opExtrude","CAP_FACE",FACE,{"disambiguationData":[OSD([sQuery(id+"F8.wireOp",EDGE,"E22.6.0"),sQuery(id+"F8.wireOp",EDGE,"E22.6.1"),sQuery(id+"F8.wireOp",EDGE,"E22.6.2"),sQuery(id+"F8.wireOp",EDGE,"E22.6.3"),sQuery(id+"F8.wireOp",EDGE,"E22.6.4"),sQuery(id+"F8.wireOp",EDGE,"E22.6.5"),sQuery(id+"F8.wireOp",EDGE,"E22.6.6"),sQuery(id+"F8.wireOp",EDGE,"E22.6.7")])],"isStart":false}),makeQuery(id+"F9.opExtrude","CAP_FACE",FACE,{"disambiguationData":[OSD([sQuery(id+"F8.wireOp",EDGE,"E22.8.0"),sQuery(id+"F8.wireOp",EDGE,"E22.8.1"),sQuery(id+"F8.wireOp",EDGE,"E22.8.2"),sQuery(id+"F8.wireOp",EDGE,"E22.8.3"),sQuery(id+"F8.wireOp",EDGE,"E22.8.4"),sQuery(id+"F8.wireOp",EDGE,"E22.8.5"),sQuery(id+"F8.wireOp",EDGE,"E22.8.6"),sQuery(id+"F8.wireOp",EDGE,"E22.8.7")])],"isStart":false}),makeQuery(id+"F9.opExtrude","CAP_FACE",FACE,{"disambiguationData":[OSD([sQuery(id+"F8.wireOp",EDGE,"E22.10.0"),sQuery(id+"F8.wireOp",EDGE,"E22.10.1"),sQuery(id+"F8.wireOp",EDGE,"E22.10.2"),sQuery(id+"F8.wireOp",EDGE,"E22.10.3"),sQuery(id+"F8.wireOp",EDGE,"E22.10.4"),sQuery(id+"F8.wireOp",EDGE,"E22.10.5"),sQuery(id+"F8.wireOp",EDGE,"E22.10.6"),sQuery(id+"F8.wireOp",EDGE,"E22.10.7")])],"isStart":false}),makeQuery(id+"F9.opExtrude","CAP_FACE",FACE,{"disambiguationData":[OSD([sQuery(id+"F8.wireOp",EDGE,"E22.13.0"),sQuery(id+"F8.wireOp",EDGE,"E22.13.1"),sQuery(id+"F8.wireOp",EDGE,"E22.13.2"),sQuery(id+"F8.wireOp",EDGE,"E22.13.3"),sQuery(id+"F8.wireOp",EDGE,"E22.13.4"),sQuery(id+"F8.wireOp",EDGE,"E22.13.5"),sQuery(id+"F8.wireOp",EDGE,"E22.13.6"),sQuery(id+"F8.wireOp",EDGE,"E22.13.7")])],"isStart":false}),makeQuery(id+"F10.opExtrude","CAP_FACE",FACE,{"disambiguationData":[OSD([sQuery(id+"F0.wireOp",EDGE,"E0"),sQuery(id+"F0.wireOp",EDGE,"E3"),sQuery(id+"F0.wireOp",EDGE,"E4"),sQuery(id+"F0.wireOp",EDGE,"E5.MirrorCS"),sQuery(id+"F0.wireOp",EDGE,"E6.MirrorCS"),sQuery(id+"F0.wireOp",EDGE,"E9.1.0"),sQuery(id+"F0.wireOp",EDGE,"E9.1.1"),sQuery(id+"F0.wireOp",EDGE,"E9.1.2"),sQuery(id+"F0.wireOp",EDGE,"E9.1.3"),sQuery(id+"F0.wireOp",EDGE,"E9.2.0"),sQuery(id+"F0.wireOp",EDGE,"E9.2.1"),sQuery(id+"F0.wireOp",EDGE,"E9.2.2"),sQuery(id+"F0.wireOp",EDGE,"E9.2.3"),sQuery(id+"F0.wireOp",EDGE,"E9.3.0"),sQuery(id+"F0.wireOp",EDGE,"E9.3.1"),sQuery(id+"F0.wireOp",EDGE,"E9.3.2"),sQuery(id+"F0.wireOp",EDGE,"E9.3.3"),sQuery(id+"F0.wireOp",EDGE,"E9.4.0"),sQuery(id+"F0.wireOp",EDGE,"E9.4.1"),sQuery(id+"F0.wireOp",EDGE,"E9.4.2"),sQuery(id+"F0.wireOp",EDGE,"E9.4.3"),sQuery(id+"F0.wireOp",EDGE,"E9.5.0"),sQuery(id+"F0.wireOp",EDGE,"E9.5.1"),sQuery(id+"F0.wireOp",EDGE,"E9.5.2"),sQuery(id+"F0.wireOp",EDGE,"E9.5.3"),sQuery(id+"F2.wireOp",EDGE,"E10")])],"isStart":false})]});
            extrude(context, id + "F14", {"entities" : qUnion([Q0]), "operationType" : NewBodyOperationType.ADD, "endBound" : BoundingType.UP_TO_SURFACE, "oppositeDirection" : true, "depth" : 25.4 * mm, "endBoundEntityFace" : qUnion([Q1]), "offsetDistance" : 25.4 * mm});
        }
    });
